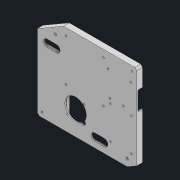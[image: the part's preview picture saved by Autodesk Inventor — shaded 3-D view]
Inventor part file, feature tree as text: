
AUTODESK INVENTOR PART (.ipt)
format: ipt  version: 2022 (Build 260153000, 153)  size: 529,408 bytes
history: native  units: mm
features: reference x14, extrude x9, sketch x9, other x6, fillet x5, hole x4, projected_geometry x3, imported_body x1, chamfer x1
ambient origin geometry x8: Origin, YZ Plane, XZ Plane, XY Plane, X Axis, Y Axis, Z Axis, Center Point
bodies: Solid1 (feature_tree)
feature tree (52):
  imported_body  "BASE"
  extrude  "Extrusion1"  Depth=150.0mm
  extrude  "Extrusion2"  Depth=10.0mm
  fillet  "Fillet1"  Radius=200.0mm
  hole  "Hole1"  [1 undecoded]
  hole  "wall mount"  [1 undecoded]
  hole  "cover mount"  [1 undecoded]
  chamfer  "Chamfer1"  Distance=10.0mm
  extrude  "Extrusion4"  Depth=2.0mm TaperAngle=45.0deg
  extrude  "Extrusion5"  Depth=2.0mm
  hole  "Hole4"  [1 undecoded]
  extrude  "speaker"  Depth=10.0mm TaperAngle=0.0deg
  sketch  "Sketch19"  dims[d75=10.0mm]
  extrude  "Extrusion8"  Depth=2.0mm
  fillet  "Fillet3"  Radius=16.0mm
  fillet  "Fillet2"  Radius=6.5mm
  extrude  "Extrusion10"  Depth=2.0mm
  extrude  "Extrusion7"  Depth=10.0mm TaperAngle=0.0deg
  extrude  "Extrusion11"  Depth=2.0mm
  fillet  "Fillet4"  Radius=50.0mm
  fillet  "Fillet5"  Radius=80.0mm
  sketch  "Sketch9"  dims[d4=60.0deg d5=150.0mm]
  reference  "Reference13"
  reference  "Reference14"
  reference  "Reference15"
  reference  "Reference16"
  reference  "Reference17"
  reference  "Reference18"
  reference  "Reference19"
  reference  "Reference20"
  reference  "Reference21"
  reference  "Reference22"
  projected_geometry  "Projected Loop2"
  reference  "Reference23"
  reference  "Reference24"
  sketch  "Sketch10"  dims[d6=10.0mm d7=180.0mm d8=200.0mm]
  projected_geometry  "Projected Loop3"
  sketch  "Sketch11"  dims[d10=2.0mm d11=2.0mm d12=0.0mm]
  sketch  "Sketch12"  dims[d13=2.0mm d14=0.0mm d19=10.0mm d20=0.0mm]
  sketch  "Sketch15"  dims[d49=3.6mm d50=6.0mm d51=6.5mm d52=3.4mm d53=90.0deg d54=8.0mm d55=20.594885mm]
  sketch  "Sketch16"  dims[d60=4.8mm d61=6.0mm d62=8.0mm d63=4.6mm d64=90.0deg d65=8.0mm d66=20.594885mm]
  reference  "Reference25"
  reference  "Reference26"
  sketch  "Sketch17"  dims[d67=3.6mm d68=6.0mm d69=6.5mm d70=3.4mm d71=90.0deg d72=8.0mm d73=20.594885mm d74=10.0mm]
  projected_geometry  "Projected Loop4"
  sketch  "Sketch22"  dims[d76=10.0mm d77=10.0mm d78=4.0mm d79=2.0mm d80=45.0deg d81=5.0mm d82=5.0mm d83=10.0mm d84=0.0mm d89=16.0mm d90=16.0mm d91=6.5mm d92=6.5mm d93=10.0mm d94=0.0mm d95=45.0mm d96=50.0mm d97=80.0mm d98=0.0mm d99=0.0mm d100=3.6mm d101=6.0mm d102=6.5mm d103=3.4mm d104=90.0deg d105=8.0mm d106=20.594885mm d107=5.0mm d108=15.0mm d109=20.0mm d110=130.0mm d111=20.0mm d112=10.0mm d113=0.0mm d116=150.0mm d117=150.0mm d118=20.0mm d119=15.0mm d120=30.0mm d121=140.0mm d122=4.0mm d123=60.0deg d124=60.0deg d125=4.0mm d126=15.0mm d127=20.0mm d135=10.0mm d136=0.0mm d137=4.0mm d141=3.0mm d142=120.0mm d143=52.0mm d148=9.0mm d149=0.0mm d150=0.0mm d151=40.0mm d152=40.0mm d153=40.0mm d154=40.0mm d155=8.0mm d156=0.0mm d157=3.0mm d158=9.0mm d159=9.0mm d160=9.0mm d161=2.0mm d162=9.0mm d163=0.5mm d164=0.872665mm]
  parser-record x1  (decoder bookkeeping rows leaked as tree rows — omitted from the tree; the rows remain in map.json)
  other  "Ensamble.iam"
  other  "mainboard:1"
  other  "4_Relay_module_Simplify_1:1"
  other  "Ardi_UNO:1"
  other  "speaker:1"
note: 4 required parameter values undecoded (feature->parameter linkage not recoverable at this tier; creation-order binding heuristic only, values carry confidence <= 0.55)
note: 1 file-system path scrubbed to <path> (originals preserved in map.json)
